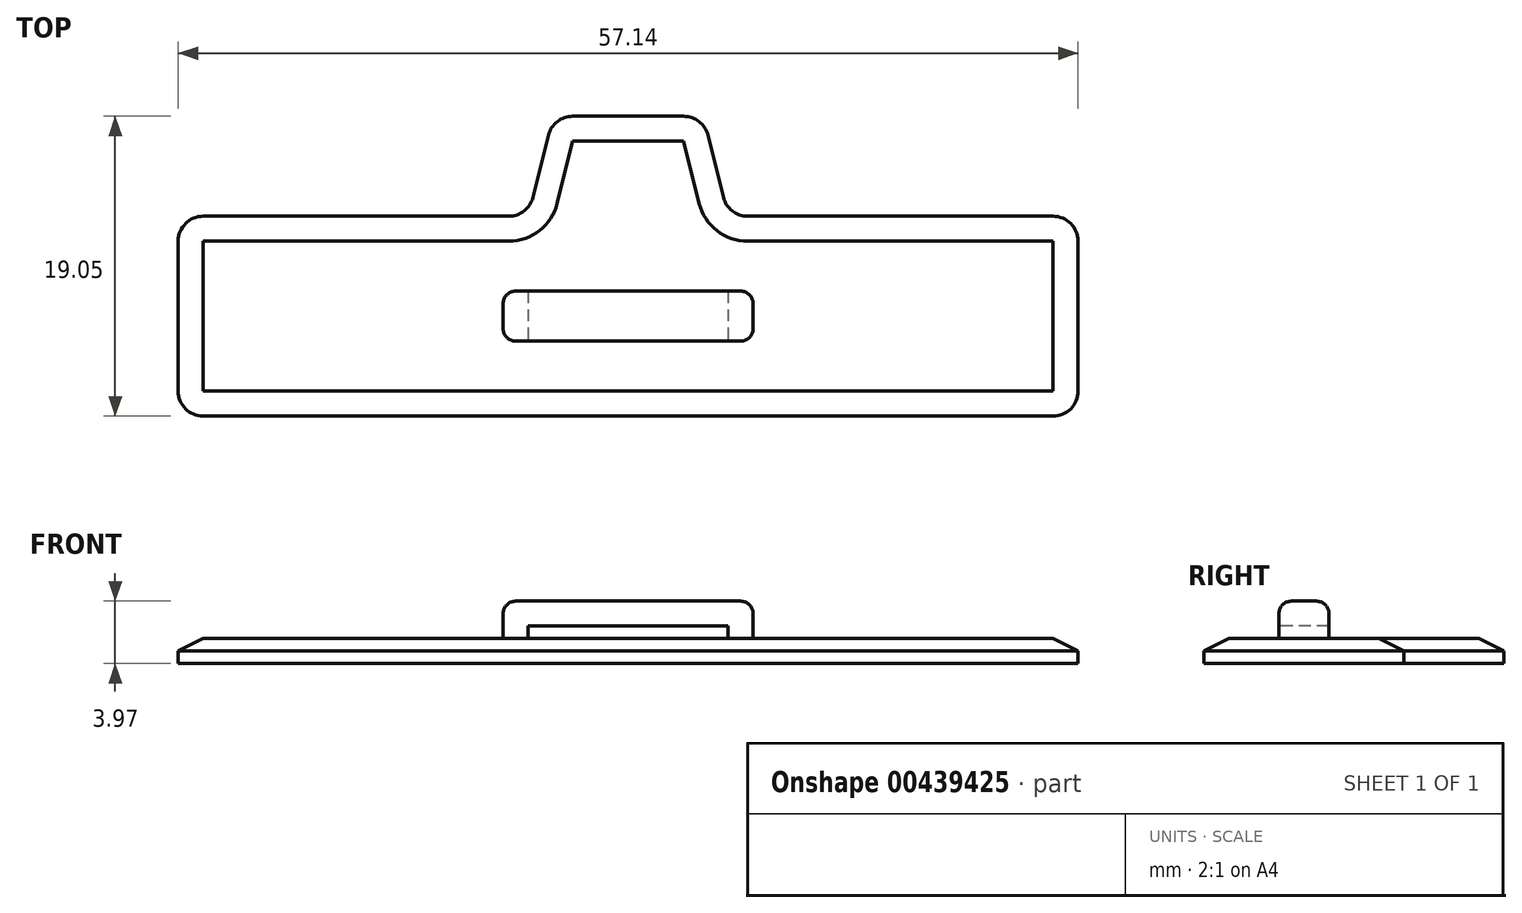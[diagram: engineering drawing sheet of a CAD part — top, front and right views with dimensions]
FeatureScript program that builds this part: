
annotation { "Feature Type Name" : "Feature", "Feature Type Description" : "" }
export const myFeature = defineFeature(function(context is Context, id is Id, definition is map)
    precondition{}
    {
        {
            var Q0;
            Q0=qCreatedBy(makeId("Top.planeOp"),FACE);
            var sketch = newSketch(context, id + "F0", { "sketchPlane" : qUnion([Q0])});
            skLineSegment(sketch, "E0.bottom", {"start": v(28.58, 6.35) * mm, "end": v(6.35, 6.35) * mm});
            skLineSegment(sketch, "E0.top", {"start": v(28.58, -6.35) * mm, "end": v(-28.58, -6.35) * mm});
            skLineSegment(sketch, "E0.left", {"start": v(28.58, 6.35) * mm, "end": v(28.58, -6.35) * mm});
            skLineSegment(sketch, "E0.right", {"start": v(-28.58, 6.35) * mm, "end": v(-28.58, -6.35) * mm});
            skPoint(sketch, "E0.middle", {"position": v(0, 0) * mm});
            skLineSegment(sketch, "E1.top", {"start": v(4.76, 12.7) * mm, "end": v(-4.76, 12.7) * mm});
            skLineSegment(sketch, "E2", {"start": v(-4.76, 12.7) * mm, "end": v(-6.35, 6.35) * mm});
            skLineSegment(sketch, "E3", {"start": v(4.76, 12.7) * mm, "end": v(6.35, 6.35) * mm});
            skLineSegment(sketch, "E4.trimOffspring", {"start": v(-6.35, 6.35) * mm, "end": v(-28.58, 6.35) * mm});
            skLineSegment(sketch, "E5", {"start": v(0, -6.35) * mm, "end": v(0, 12.7) * mm, "construction": true});
            skSolve(sketch);
        }
        {
            var Q0;
            Q0 = qSketchRegion(id + "F0", true);
            extrude(context, id + "F1", {"entities" : qUnion([Q0]), "depth" : 1.59 * mm});
        }
        {
            var Q0;
            Q0=makeQuery(id+"F1.opExtrude","CAP_FACE",FACE,{"disambiguationData":[OSD([sQuery(id+"F0.wireOp",EDGE,"E0.bottom"),sQuery(id+"F0.wireOp",EDGE,"E0.top"),sQuery(id+"F0.wireOp",EDGE,"E0.left"),sQuery(id+"F0.wireOp",EDGE,"E0.right"),sQuery(id+"F0.wireOp",EDGE,"E1.top"),sQuery(id+"F0.wireOp",EDGE,"E2"),sQuery(id+"F0.wireOp",EDGE,"E3"),sQuery(id+"F0.wireOp",EDGE,"E4.trimOffspring")])],"isStart":false});
            var sketch = newSketch(context, id + "F2", { "sketchPlane" : qUnion([Q0])});
            skLineSegment(sketch, "E6.bottom", {"start": v(-7.94, 1.59) * mm, "end": v(7.94, 1.59) * mm});
            skLineSegment(sketch, "E6.top", {"start": v(-7.94, -1.59) * mm, "end": v(7.94, -1.59) * mm});
            skLineSegment(sketch, "E6.left", {"start": v(-7.94, 1.59) * mm, "end": v(-7.94, -1.59) * mm});
            skLineSegment(sketch, "E6.right", {"start": v(7.94, 1.59) * mm, "end": v(7.94, -1.59) * mm});
            skPoint(sketch, "E6.middle", {"position": v(0, 0) * mm});
            skSolve(sketch);
        }
        {
            var Q0;
            Q0 = qSketchRegion(id + "F2", true);
            extrude(context, id + "F3", {"entities" : qUnion([Q0]), "operationType" : NewBodyOperationType.ADD, "depth" : 2.38 * mm});
        }
        {
            var Q0;
            Q0=makeQuery(id+"F3.opExtrude","CAP_FACE",FACE,{"disambiguationData":[OSD([sQuery(id+"F2.wireOp",EDGE,"E6.bottom"),sQuery(id+"F2.wireOp",EDGE,"E6.top"),sQuery(id+"F2.wireOp",EDGE,"E6.left"),sQuery(id+"F2.wireOp",EDGE,"E6.right")])],"isStart":false});
            cPlane(context, id + "F4", {"entities" : qUnion([Q0]), "cplaneType" : CPlaneType.OFFSET, "offset" : 1.59 * mm, "oppositeDirection" : true, "width" : 152.4 * mm, "height" : 152.4 * mm});
        }
        {
            var Q0;
            Q0=qCreatedBy(id+"F4.planeOp",FACE);
            var sketch = newSketch(context, id + "F5", { "sketchPlane" : qUnion([Q0])});
            skLineSegment(sketch, "E7.0.1", {"start": v(-6.35, -1.59) * mm, "end": v(6.35, -1.59) * mm});
            skLineSegment(sketch, "E7.0.3", {"start": v(6.35, 1.59) * mm, "end": v(-6.35, 1.59) * mm});
            skLineSegment(sketch, "E8", {"start": v(-6.35, 1.59) * mm, "end": v(-6.35, -1.59) * mm});
            skLineSegment(sketch, "E9", {"start": v(6.35, 1.59) * mm, "end": v(6.35, -1.59) * mm});
            skLineSegment(sketch, "E10", {"start": v(0, 1.59) * mm, "end": v(0, -1.59) * mm, "construction": true});
            skSolve(sketch);
        }
        {
            var Q0;
            Q0 = qSketchRegion(id + "F5", true);
            extrude(context, id + "F6", {"entities" : qUnion([Q0]), "operationType" : NewBodyOperationType.REMOVE, "oppositeDirection" : true, "depth" : 0.8 * mm});
        }
        {
            var Q0;
            Q0=makeQuery(id+"F1.opExtrude","SWEPT_EDGE",EDGE,{"disambiguationData":[OSD([sQuery(id+"F0.wireOp",EDGE,"E0.top"),sQuery(id+"F0.wireOp",EDGE,"E0.right")])]});
            var Q1;
            Q1=makeQuery(id+"F1.opExtrude","SWEPT_EDGE",EDGE,{"disambiguationData":[OSD([sQuery(id+"F0.wireOp",EDGE,"E0.top"),sQuery(id+"F0.wireOp",EDGE,"E0.left")])]});
            var Q2;
            Q2=makeQuery(id+"F1.opExtrude","SWEPT_EDGE",EDGE,{"disambiguationData":[OSD([sQuery(id+"F0.wireOp",EDGE,"E0.bottom"),sQuery(id+"F0.wireOp",EDGE,"E0.left")])]});
            var Q3;
            Q3=makeQuery(id+"F1.opExtrude","SWEPT_EDGE",EDGE,{"disambiguationData":[OSD([sQuery(id+"F0.wireOp",EDGE,"E1.top"),sQuery(id+"F0.wireOp",EDGE,"E3")])]});
            var Q4;
            Q4=makeQuery(id+"F1.opExtrude","SWEPT_EDGE",EDGE,{"disambiguationData":[OSD([sQuery(id+"F0.wireOp",EDGE,"E0.right"),sQuery(id+"F0.wireOp",EDGE,"E4.trimOffspring")])]});
            var Q5;
            Q5=makeQuery(id+"F1.opExtrude","SWEPT_EDGE",EDGE,{"disambiguationData":[OSD([sQuery(id+"F0.wireOp",EDGE,"E1.top"),sQuery(id+"F0.wireOp",EDGE,"E2")])]});
            var Q6;
            Q6=makeQuery(id+"F1.opExtrude","SWEPT_EDGE",EDGE,{"disambiguationData":[OSD([sQuery(id+"F0.wireOp",EDGE,"E2"),sQuery(id+"F0.wireOp",EDGE,"E4.trimOffspring")])]});
            var Q7;
            Q7=makeQuery(id+"F1.opExtrude","SWEPT_EDGE",EDGE,{"disambiguationData":[OSD([sQuery(id+"F0.wireOp",EDGE,"E0.bottom"),sQuery(id+"F0.wireOp",EDGE,"E3")])]});
            fillet(context, id + "F7", {"entities" : qUnion([Q0, Q1, Q2, Q3, Q4, Q5, Q6, Q7]), "radius" : 1.59 * mm, "tangentPropagation" : true, "allowEdgeOverflow" : false});
        }
        {
            var Q0;
            Q0=makeQuery(id+"F3.opExtrude","CAP_EDGE",EDGE,{"disambiguationData":[OSD([sQuery(id+"F2.wireOp",EDGE,"E6.right")])],"isStart":true});
            var Q1;
            Q1=makeQuery(id+"F3.opExtrude","CAP_EDGE",EDGE,{"disambiguationData":[OSD([sQuery(id+"F2.wireOp",EDGE,"E6.right")])],"isStart":false});
            var Q2;
            Q2=makeQuery(id+"F3.opExtrude","CAP_EDGE",EDGE,{"disambiguationData":[OSD([sQuery(id+"F2.wireOp",EDGE,"E6.left")])],"isStart":false});
            var Q3;
            Q3=makeQuery(id+"F3.opExtrude","CAP_EDGE",EDGE,{"disambiguationData":[OSD([sQuery(id+"F2.wireOp",EDGE,"E6.left")])],"isStart":true});
            fillet(context, id + "F8", {"entities" : qUnion([Q0, Q1, Q2, Q3]), "radius" : 0.8 * mm, "tangentPropagation" : true, "allowEdgeOverflow" : false});
        }
        {
            var Q0;
            Q0=makeQuery(id+"F3.opExtrude","CAP_EDGE",EDGE,{"disambiguationData":[OSD([sQuery(id+"F2.wireOp",EDGE,"E6.bottom")])],"isStart":false});
            var Q1;
            Q1=makeQuery(id+"F6.boolean.opBoolean","COPY",EDGE,{"derivedFrom":makeQuery(id+"F6.opExtrude","CAP_EDGE",EDGE,{"disambiguationData":[OSD([sQuery(id+"F5.wireOp",EDGE,"E7.0.3")])],"isStart":true})});
            var Q2;
            Q2=makeQuery(id+"F3.opExtrude","CAP_EDGE",EDGE,{"disambiguationData":[OSD([sQuery(id+"F2.wireOp",EDGE,"E6.top")])],"isStart":false});
            var Q3;
            Q3=makeQuery(id+"F6.boolean.opBoolean","COPY",EDGE,{"derivedFrom":makeQuery(id+"F6.opExtrude","CAP_EDGE",EDGE,{"disambiguationData":[OSD([sQuery(id+"F5.wireOp",EDGE,"E7.0.1")])],"isStart":true})});
            fillet(context, id + "F9", {"entities" : qUnion([Q0, Q1, Q2, Q3]), "radius" : 0.8 * mm, "tangentPropagation" : true, "allowEdgeOverflow" : false});
        }
        {
            var Q0;
            Q0=makeQuery(id+"F1.opExtrude","CAP_EDGE",EDGE,{"disambiguationData":[OSD([sQuery(id+"F0.wireOp",EDGE,"E0.bottom")])],"isStart":false});
            chamfer(context, id + "F10", {"entities" : qUnion([Q0]), "chamferType" : ChamferType.TWO_OFFSETS, "width1" : 1.59 * mm, "oppositeDirection" : false, "width2" : 0.8 * mm, "tangentPropagation" : true});
        }
    });
